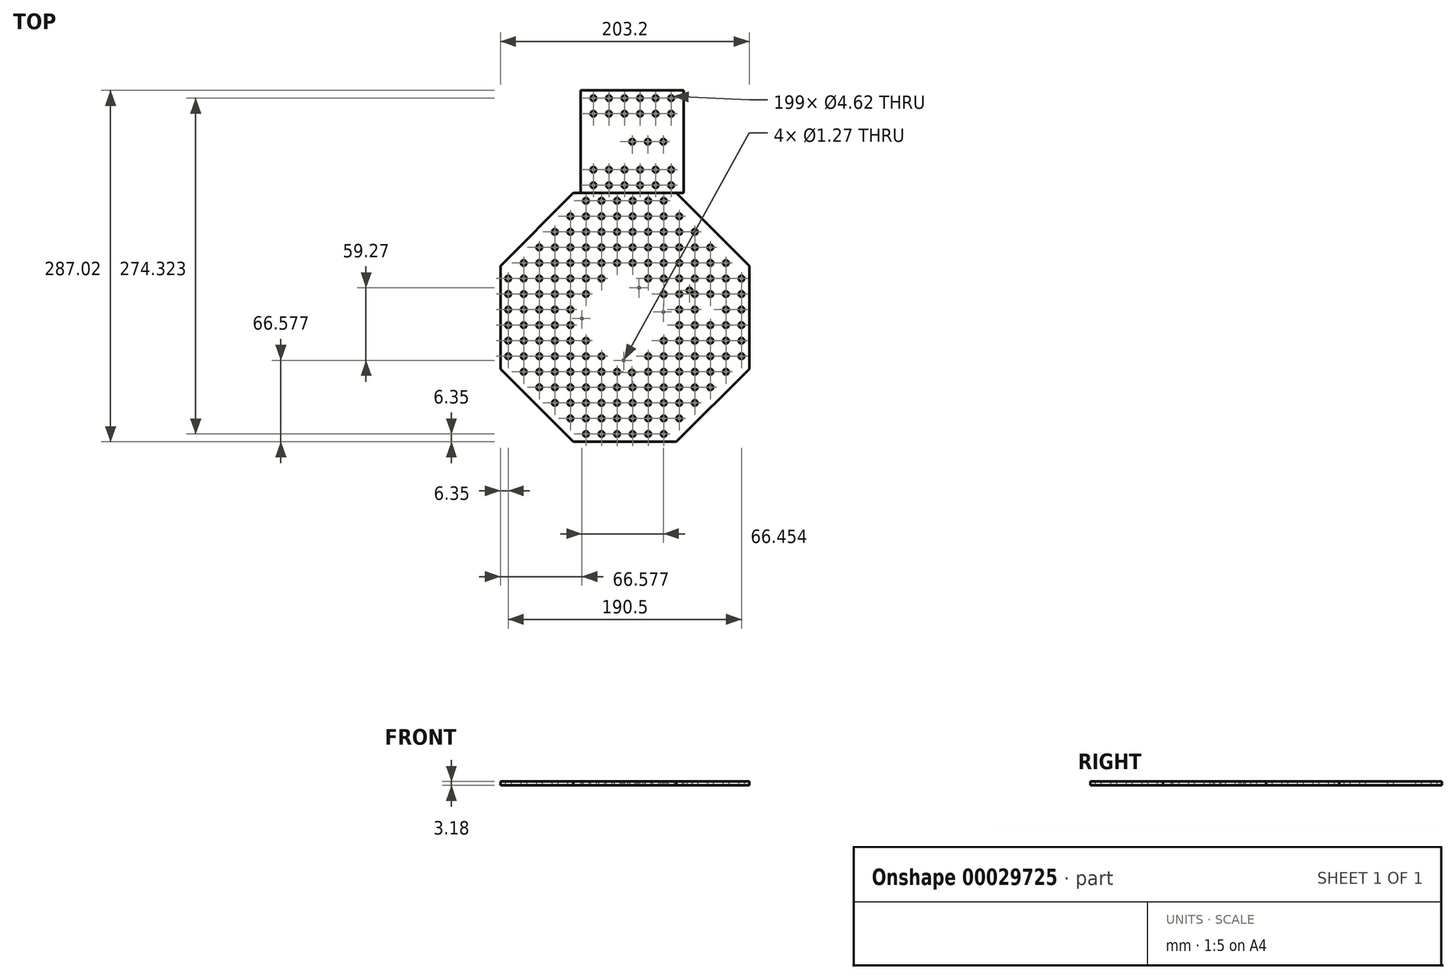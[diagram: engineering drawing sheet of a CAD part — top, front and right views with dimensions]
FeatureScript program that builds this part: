
annotation { "Feature Type Name" : "Feature", "Feature Type Description" : "" }
export const myFeature = defineFeature(function(context is Context, id is Id, definition is map)
    precondition{}
    {
        {
            var Q0;
            Q0=qCreatedBy(makeId("Top.planeOp"),FACE);
            var sketch = newSketch(context, id + "F0", { "sketchPlane" : qUnion([Q0])});
            skLineSegment(sketch, "E0", {"start": v(-101.6, 42.08) * mm, "end": v(-42.08, 101.6) * mm});
            skLineSegment(sketch, "E1", {"start": v(-42.08, 101.6) * mm, "end": v(42.08, 101.6) * mm});
            skLineSegment(sketch, "E2", {"start": v(42.08, 101.6) * mm, "end": v(101.6, 42.08) * mm});
            skLineSegment(sketch, "E3", {"start": v(101.6, 42.08) * mm, "end": v(101.6, -42.08) * mm});
            skLineSegment(sketch, "E4", {"start": v(101.6, -42.08) * mm, "end": v(42.08, -101.6) * mm});
            skLineSegment(sketch, "E5", {"start": v(42.08, -101.6) * mm, "end": v(-42.08, -101.6) * mm});
            skLineSegment(sketch, "E6", {"start": v(-42.08, -101.6) * mm, "end": v(-101.6, -42.08) * mm});
            skLineSegment(sketch, "E7", {"start": v(-101.6, -42.08) * mm, "end": v(-101.6, 42.08) * mm});
            skCircle(sketch, "E8.0.5.0", {"center": v(-95.25, 31.75) * mm, "radius": 2.31 * mm});
            skCircle(sketch, "E8.0.6.0", {"center": v(-95.25, 19.05) * mm, "radius": 2.31 * mm});
            skCircle(sketch, "E8.0.7.0", {"center": v(-95.25, 6.35) * mm, "radius": 2.31 * mm});
            skCircle(sketch, "E8.0.8.0", {"center": v(-95.25, -6.35) * mm, "radius": 2.31 * mm});
            skCircle(sketch, "E8.0.9.0", {"center": v(-95.25, -19.05) * mm, "radius": 2.31 * mm});
            skCircle(sketch, "E8.0.10.0", {"center": v(-95.25, -31.75) * mm, "radius": 2.31 * mm});
            skCircle(sketch, "E8.1.4.0", {"center": v(-82.55, 44.45) * mm, "radius": 2.31 * mm});
            skCircle(sketch, "E8.1.5.0", {"center": v(-82.55, 31.75) * mm, "radius": 2.31 * mm});
            skCircle(sketch, "E8.1.6.0", {"center": v(-82.55, 19.05) * mm, "radius": 2.31 * mm});
            skCircle(sketch, "E8.1.7.0", {"center": v(-82.55, 6.35) * mm, "radius": 2.31 * mm});
            skCircle(sketch, "E8.1.8.0", {"center": v(-82.55, -6.35) * mm, "radius": 2.31 * mm});
            skCircle(sketch, "E8.1.9.0", {"center": v(-82.55, -19.05) * mm, "radius": 2.31 * mm});
            skCircle(sketch, "E8.1.10.0", {"center": v(-82.55, -31.75) * mm, "radius": 2.31 * mm});
            skCircle(sketch, "E8.1.11.0", {"center": v(-82.55, -44.45) * mm, "radius": 2.31 * mm});
            skCircle(sketch, "E8.2.3.0", {"center": v(-69.85, 57.15) * mm, "radius": 2.31 * mm});
            skCircle(sketch, "E8.2.4.0", {"center": v(-69.85, 44.45) * mm, "radius": 2.31 * mm});
            skCircle(sketch, "E8.2.5.0", {"center": v(-69.85, 31.75) * mm, "radius": 2.31 * mm});
            skCircle(sketch, "E8.2.6.0", {"center": v(-69.85, 19.05) * mm, "radius": 2.31 * mm});
            skCircle(sketch, "E8.2.7.0", {"center": v(-69.85, 6.35) * mm, "radius": 2.31 * mm});
            skCircle(sketch, "E8.2.8.0", {"center": v(-69.85, -6.35) * mm, "radius": 2.31 * mm});
            skCircle(sketch, "E8.2.9.0", {"center": v(-69.85, -19.05) * mm, "radius": 2.31 * mm});
            skCircle(sketch, "E8.2.10.0", {"center": v(-69.85, -31.75) * mm, "radius": 2.31 * mm});
            skCircle(sketch, "E8.2.11.0", {"center": v(-69.85, -44.45) * mm, "radius": 2.31 * mm});
            skCircle(sketch, "E8.2.12.0", {"center": v(-69.85, -57.15) * mm, "radius": 2.31 * mm});
            skCircle(sketch, "E8.3.2.0", {"center": v(-57.15, 69.85) * mm, "radius": 2.31 * mm});
            skCircle(sketch, "E8.3.3.0", {"center": v(-57.15, 57.15) * mm, "radius": 2.31 * mm});
            skCircle(sketch, "E8.3.4.0", {"center": v(-57.15, 44.45) * mm, "radius": 2.31 * mm});
            skCircle(sketch, "E8.3.5.0", {"center": v(-57.15, 31.75) * mm, "radius": 2.31 * mm});
            skCircle(sketch, "E8.3.6.0", {"center": v(-57.15, 19.05) * mm, "radius": 2.31 * mm});
            skCircle(sketch, "E8.3.7.0", {"center": v(-57.15, 6.35) * mm, "radius": 2.31 * mm});
            skCircle(sketch, "E8.3.8.0", {"center": v(-57.15, -6.35) * mm, "radius": 2.31 * mm});
            skCircle(sketch, "E8.3.9.0", {"center": v(-57.15, -19.05) * mm, "radius": 2.31 * mm});
            skCircle(sketch, "E8.3.10.0", {"center": v(-57.15, -31.75) * mm, "radius": 2.31 * mm});
            skCircle(sketch, "E8.3.11.0", {"center": v(-57.15, -44.45) * mm, "radius": 2.31 * mm});
            skCircle(sketch, "E8.3.12.0", {"center": v(-57.15, -57.15) * mm, "radius": 2.31 * mm});
            skCircle(sketch, "E8.3.13.0", {"center": v(-57.15, -69.85) * mm, "radius": 2.31 * mm});
            skCircle(sketch, "E8.4.1.0", {"center": v(-44.45, 82.55) * mm, "radius": 2.31 * mm});
            skCircle(sketch, "E8.4.2.0", {"center": v(-44.45, 69.85) * mm, "radius": 2.31 * mm});
            skCircle(sketch, "E8.4.3.0", {"center": v(-44.45, 57.15) * mm, "radius": 2.31 * mm});
            skCircle(sketch, "E8.4.4.0", {"center": v(-44.45, 44.45) * mm, "radius": 2.31 * mm});
            skCircle(sketch, "E8.4.5.0", {"center": v(-44.45, 31.75) * mm, "radius": 2.31 * mm});
            skCircle(sketch, "E8.4.6.0", {"center": v(-44.45, 19.05) * mm, "radius": 2.31 * mm});
            skCircle(sketch, "E8.4.7.0", {"center": v(-44.45, 6.35) * mm, "radius": 2.31 * mm});
            skCircle(sketch, "E8.4.8.0", {"center": v(-44.45, -6.35) * mm, "radius": 2.31 * mm});
            skCircle(sketch, "E8.4.9.0", {"center": v(-44.45, -19.05) * mm, "radius": 2.31 * mm});
            skCircle(sketch, "E8.4.10.0", {"center": v(-44.45, -31.75) * mm, "radius": 2.31 * mm});
            skCircle(sketch, "E8.4.11.0", {"center": v(-44.45, -44.45) * mm, "radius": 2.31 * mm});
            skCircle(sketch, "E8.4.12.0", {"center": v(-44.45, -57.15) * mm, "radius": 2.31 * mm});
            skCircle(sketch, "E8.4.13.0", {"center": v(-44.45, -69.85) * mm, "radius": 2.31 * mm});
            skCircle(sketch, "E8.4.14.0", {"center": v(-44.45, -82.55) * mm, "radius": 2.31 * mm});
            skCircle(sketch, "E8.5.0.0", {"center": v(-31.75, 95.25) * mm, "radius": 2.31 * mm});
            skCircle(sketch, "E8.5.1.0", {"center": v(-31.75, 82.55) * mm, "radius": 2.31 * mm});
            skCircle(sketch, "E8.5.2.0", {"center": v(-31.75, 69.85) * mm, "radius": 2.31 * mm});
            skCircle(sketch, "E8.5.3.0", {"center": v(-31.75, 57.15) * mm, "radius": 2.31 * mm});
            skCircle(sketch, "E8.5.4.0", {"center": v(-31.75, 44.45) * mm, "radius": 2.31 * mm});
            skCircle(sketch, "E8.5.5.0", {"center": v(-31.75, 31.75) * mm, "radius": 2.31 * mm});
            skCircle(sketch, "E8.5.6.0", {"center": v(-31.75, 19.05) * mm, "radius": 2.31 * mm});
            skCircle(sketch, "E8.5.9.0", {"center": v(-31.75, -19.05) * mm, "radius": 2.31 * mm});
            skCircle(sketch, "E8.5.10.0", {"center": v(-31.75, -31.75) * mm, "radius": 2.31 * mm});
            skCircle(sketch, "E8.5.11.0", {"center": v(-31.75, -44.45) * mm, "radius": 2.31 * mm});
            skCircle(sketch, "E8.5.12.0", {"center": v(-31.75, -57.15) * mm, "radius": 2.31 * mm});
            skCircle(sketch, "E8.5.13.0", {"center": v(-31.75, -69.85) * mm, "radius": 2.31 * mm});
            skCircle(sketch, "E8.5.14.0", {"center": v(-31.75, -82.55) * mm, "radius": 2.31 * mm});
            skCircle(sketch, "E8.5.15.0", {"center": v(-31.75, -95.25) * mm, "radius": 2.31 * mm});
            skCircle(sketch, "E8.6.0.0", {"center": v(-19.05, 95.25) * mm, "radius": 2.31 * mm});
            skCircle(sketch, "E8.6.1.0", {"center": v(-19.05, 82.55) * mm, "radius": 2.31 * mm});
            skCircle(sketch, "E8.6.2.0", {"center": v(-19.05, 69.85) * mm, "radius": 2.31 * mm});
            skCircle(sketch, "E8.6.3.0", {"center": v(-19.05, 57.15) * mm, "radius": 2.31 * mm});
            skCircle(sketch, "E8.6.4.0", {"center": v(-19.05, 44.45) * mm, "radius": 2.31 * mm});
            skCircle(sketch, "E8.6.5.0", {"center": v(-19.05, 31.75) * mm, "radius": 2.31 * mm});
            skCircle(sketch, "E8.6.10.0", {"center": v(-19.05, -31.75) * mm, "radius": 2.31 * mm});
            skCircle(sketch, "E8.6.11.0", {"center": v(-19.05, -44.45) * mm, "radius": 2.31 * mm});
            skCircle(sketch, "E8.6.12.0", {"center": v(-19.05, -57.15) * mm, "radius": 2.31 * mm});
            skCircle(sketch, "E8.6.13.0", {"center": v(-19.05, -69.85) * mm, "radius": 2.31 * mm});
            skCircle(sketch, "E8.6.14.0", {"center": v(-19.05, -82.55) * mm, "radius": 2.31 * mm});
            skCircle(sketch, "E8.6.15.0", {"center": v(-19.05, -95.25) * mm, "radius": 2.31 * mm});
            skCircle(sketch, "E8.7.0.0", {"center": v(-6.35, 95.25) * mm, "radius": 2.31 * mm});
            skCircle(sketch, "E8.7.1.0", {"center": v(-6.35, 82.55) * mm, "radius": 2.31 * mm});
            skCircle(sketch, "E8.7.2.0", {"center": v(-6.35, 69.85) * mm, "radius": 2.31 * mm});
            skCircle(sketch, "E8.7.3.0", {"center": v(-6.35, 57.15) * mm, "radius": 2.31 * mm});
            skCircle(sketch, "E8.7.4.0", {"center": v(-6.35, 44.45) * mm, "radius": 2.31 * mm});
            skCircle(sketch, "E8.7.11.0", {"center": v(-6.35, -44.45) * mm, "radius": 2.31 * mm});
            skCircle(sketch, "E8.7.12.0", {"center": v(-6.35, -57.15) * mm, "radius": 2.31 * mm});
            skCircle(sketch, "E8.7.13.0", {"center": v(-6.35, -69.85) * mm, "radius": 2.31 * mm});
            skCircle(sketch, "E8.7.14.0", {"center": v(-6.35, -82.55) * mm, "radius": 2.31 * mm});
            skCircle(sketch, "E8.7.15.0", {"center": v(-6.35, -95.25) * mm, "radius": 2.31 * mm});
            skCircle(sketch, "E8.8.0.0", {"center": v(6.35, 95.25) * mm, "radius": 2.31 * mm});
            skCircle(sketch, "E8.8.1.0", {"center": v(6.35, 82.55) * mm, "radius": 2.31 * mm});
            skCircle(sketch, "E8.8.2.0", {"center": v(6.35, 69.85) * mm, "radius": 2.31 * mm});
            skCircle(sketch, "E8.8.3.0", {"center": v(6.35, 57.15) * mm, "radius": 2.31 * mm});
            skCircle(sketch, "E8.8.4.0", {"center": v(6.35, 44.45) * mm, "radius": 2.31 * mm});
            skCircle(sketch, "E8.8.11.0", {"center": v(5.77, -44.96) * mm, "radius": 2.31 * mm});
            skCircle(sketch, "E8.8.12.0", {"center": v(6.35, -57.15) * mm, "radius": 2.31 * mm});
            skCircle(sketch, "E8.8.13.0", {"center": v(6.35, -69.85) * mm, "radius": 2.31 * mm});
            skCircle(sketch, "E8.8.14.0", {"center": v(6.35, -82.55) * mm, "radius": 2.31 * mm});
            skCircle(sketch, "E8.8.15.0", {"center": v(6.35, -95.25) * mm, "radius": 2.31 * mm});
            skCircle(sketch, "E8.9.0.0", {"center": v(19.05, 95.25) * mm, "radius": 2.31 * mm});
            skCircle(sketch, "E8.9.1.0", {"center": v(19.05, 82.55) * mm, "radius": 2.31 * mm});
            skCircle(sketch, "E8.9.2.0", {"center": v(19.05, 69.85) * mm, "radius": 2.31 * mm});
            skCircle(sketch, "E8.9.3.0", {"center": v(19.05, 57.15) * mm, "radius": 2.31 * mm});
            skCircle(sketch, "E8.9.4.0", {"center": v(19.05, 44.45) * mm, "radius": 2.31 * mm});
            skCircle(sketch, "E8.9.5.0", {"center": v(19.05, 31.75) * mm, "radius": 2.31 * mm});
            skCircle(sketch, "E8.9.10.0", {"center": v(19.05, -31.75) * mm, "radius": 2.31 * mm});
            skCircle(sketch, "E8.9.11.0", {"center": v(19.05, -44.45) * mm, "radius": 2.31 * mm});
            skCircle(sketch, "E8.9.12.0", {"center": v(19.05, -57.15) * mm, "radius": 2.31 * mm});
            skCircle(sketch, "E8.9.13.0", {"center": v(19.05, -69.85) * mm, "radius": 2.31 * mm});
            skCircle(sketch, "E8.9.14.0", {"center": v(19.05, -82.55) * mm, "radius": 2.31 * mm});
            skCircle(sketch, "E8.9.15.0", {"center": v(19.05, -95.25) * mm, "radius": 2.31 * mm});
            skCircle(sketch, "E8.10.0.0", {"center": v(31.75, 95.25) * mm, "radius": 2.31 * mm});
            skCircle(sketch, "E8.10.1.0", {"center": v(31.75, 82.55) * mm, "radius": 2.31 * mm});
            skCircle(sketch, "E8.10.2.0", {"center": v(31.75, 69.85) * mm, "radius": 2.31 * mm});
            skCircle(sketch, "E8.10.3.0", {"center": v(31.75, 57.15) * mm, "radius": 2.31 * mm});
            skCircle(sketch, "E8.10.4.0", {"center": v(31.75, 44.45) * mm, "radius": 2.31 * mm});
            skCircle(sketch, "E8.10.5.0", {"center": v(31.75, 31.75) * mm, "radius": 2.31 * mm});
            skCircle(sketch, "E8.10.6.0", {"center": v(31.75, 19.05) * mm, "radius": 2.31 * mm});
            skCircle(sketch, "E8.10.9.0", {"center": v(31.75, -19.05) * mm, "radius": 2.31 * mm});
            skCircle(sketch, "E8.10.10.0", {"center": v(31.75, -31.75) * mm, "radius": 2.31 * mm});
            skCircle(sketch, "E8.10.11.0", {"center": v(31.75, -44.45) * mm, "radius": 2.31 * mm});
            skCircle(sketch, "E8.10.12.0", {"center": v(31.75, -57.15) * mm, "radius": 2.31 * mm});
            skCircle(sketch, "E8.10.13.0", {"center": v(31.75, -69.85) * mm, "radius": 2.31 * mm});
            skCircle(sketch, "E8.10.14.0", {"center": v(31.75, -82.55) * mm, "radius": 2.31 * mm});
            skCircle(sketch, "E8.10.15.0", {"center": v(31.75, -95.25) * mm, "radius": 2.31 * mm});
            skCircle(sketch, "E8.11.1.0", {"center": v(44.45, 82.55) * mm, "radius": 2.31 * mm});
            skCircle(sketch, "E8.11.2.0", {"center": v(44.45, 69.85) * mm, "radius": 2.31 * mm});
            skCircle(sketch, "E8.11.3.0", {"center": v(44.45, 57.15) * mm, "radius": 2.31 * mm});
            skCircle(sketch, "E8.11.4.0", {"center": v(44.45, 44.45) * mm, "radius": 2.31 * mm});
            skCircle(sketch, "E8.11.5.0", {"center": v(44.45, 31.75) * mm, "radius": 2.31 * mm});
            skCircle(sketch, "E8.11.6.0", {"center": v(44.45, 19.05) * mm, "radius": 2.31 * mm});
            skCircle(sketch, "E8.11.7.0", {"center": v(44.45, 6.35) * mm, "radius": 2.31 * mm});
            skCircle(sketch, "E8.11.8.0", {"center": v(44.45, -6.35) * mm, "radius": 2.31 * mm});
            skCircle(sketch, "E8.11.9.0", {"center": v(44.45, -19.05) * mm, "radius": 2.31 * mm});
            skCircle(sketch, "E8.11.10.0", {"center": v(44.45, -31.75) * mm, "radius": 2.31 * mm});
            skCircle(sketch, "E8.11.11.0", {"center": v(44.45, -44.45) * mm, "radius": 2.31 * mm});
            skCircle(sketch, "E8.11.12.0", {"center": v(44.45, -57.15) * mm, "radius": 2.31 * mm});
            skCircle(sketch, "E8.11.13.0", {"center": v(44.45, -69.85) * mm, "radius": 2.31 * mm});
            skCircle(sketch, "E8.11.14.0", {"center": v(44.45, -82.55) * mm, "radius": 2.31 * mm});
            skCircle(sketch, "E8.12.2.0", {"center": v(57.15, 69.85) * mm, "radius": 2.31 * mm});
            skCircle(sketch, "E8.12.3.0", {"center": v(57.15, 57.15) * mm, "radius": 2.31 * mm});
            skCircle(sketch, "E8.12.4.0", {"center": v(57.15, 44.45) * mm, "radius": 2.31 * mm});
            skCircle(sketch, "E8.12.5.0", {"center": v(57.15, 31.75) * mm, "radius": 2.31 * mm});
            skCircle(sketch, "E8.12.6.0", {"center": v(57.15, 19.05) * mm, "radius": 2.31 * mm});
            skCircle(sketch, "E8.12.7.0", {"center": v(57.15, 6.35) * mm, "radius": 2.31 * mm});
            skCircle(sketch, "E8.12.8.0", {"center": v(57.15, -6.35) * mm, "radius": 2.31 * mm});
            skCircle(sketch, "E8.12.9.0", {"center": v(57.15, -19.05) * mm, "radius": 2.31 * mm});
            skCircle(sketch, "E8.12.10.0", {"center": v(57.15, -31.75) * mm, "radius": 2.31 * mm});
            skCircle(sketch, "E8.12.11.0", {"center": v(57.15, -44.45) * mm, "radius": 2.31 * mm});
            skCircle(sketch, "E8.12.12.0", {"center": v(57.15, -57.15) * mm, "radius": 2.31 * mm});
            skCircle(sketch, "E8.12.13.0", {"center": v(57.15, -69.85) * mm, "radius": 2.31 * mm});
            skCircle(sketch, "E8.13.3.0", {"center": v(69.85, 57.15) * mm, "radius": 2.31 * mm});
            skCircle(sketch, "E8.13.4.0", {"center": v(69.85, 44.45) * mm, "radius": 2.31 * mm});
            skCircle(sketch, "E8.13.5.0", {"center": v(69.85, 31.75) * mm, "radius": 2.31 * mm});
            skCircle(sketch, "E8.13.6.0", {"center": v(69.85, 19.05) * mm, "radius": 2.31 * mm});
            skCircle(sketch, "E8.13.7.0", {"center": v(52.82, 21.97) * mm, "radius": 2.31 * mm});
            skCircle(sketch, "E8.13.8.0", {"center": v(69.85, -6.35) * mm, "radius": 2.31 * mm});
            skCircle(sketch, "E8.13.9.0", {"center": v(69.85, -19.05) * mm, "radius": 2.31 * mm});
            skCircle(sketch, "E8.13.10.0", {"center": v(69.85, -31.75) * mm, "radius": 2.31 * mm});
            skCircle(sketch, "E8.13.11.0", {"center": v(69.85, -44.45) * mm, "radius": 2.31 * mm});
            skCircle(sketch, "E8.13.12.0", {"center": v(69.85, -57.15) * mm, "radius": 2.31 * mm});
            skCircle(sketch, "E8.14.4.0", {"center": v(82.55, 44.45) * mm, "radius": 2.31 * mm});
            skCircle(sketch, "E8.14.5.0", {"center": v(82.55, 31.75) * mm, "radius": 2.31 * mm});
            skCircle(sketch, "E8.14.6.0", {"center": v(82.55, 19.05) * mm, "radius": 2.31 * mm});
            skCircle(sketch, "E8.14.7.0", {"center": v(82.55, 6.35) * mm, "radius": 2.31 * mm});
            skCircle(sketch, "E8.14.8.0", {"center": v(82.55, -6.35) * mm, "radius": 2.31 * mm});
            skCircle(sketch, "E8.14.9.0", {"center": v(82.55, -19.05) * mm, "radius": 2.31 * mm});
            skCircle(sketch, "E8.14.10.0", {"center": v(82.55, -31.75) * mm, "radius": 2.31 * mm});
            skCircle(sketch, "E8.14.11.0", {"center": v(82.55, -44.45) * mm, "radius": 2.31 * mm});
            skCircle(sketch, "E8.15.5.0", {"center": v(95.25, 31.75) * mm, "radius": 2.31 * mm});
            skCircle(sketch, "E8.15.6.0", {"center": v(95.25, 19.05) * mm, "radius": 2.31 * mm});
            skCircle(sketch, "E8.15.7.0", {"center": v(95.25, 6.35) * mm, "radius": 2.31 * mm});
            skCircle(sketch, "E8.15.8.0", {"center": v(95.25, -6.35) * mm, "radius": 2.31 * mm});
            skCircle(sketch, "E8.15.9.0", {"center": v(95.25, -19.05) * mm, "radius": 2.31 * mm});
            skCircle(sketch, "E8.15.10.0", {"center": v(95.25, -31.75) * mm, "radius": 2.31 * mm});
            skPoint(sketch, "E9", {"position": v(-25.4, 88.9) * mm});
            skPoint(sketch, "E10", {"position": v(-101.6, 88.9) * mm});
            skPoint(sketch, "E11", {"position": v(-88.9, 88.9) * mm});
            skPoint(sketch, "E12", {"position": v(-71.84, -71.84) * mm});
            skPoint(sketch, "E13", {"position": v(71.84, 71.84) * mm});
            skPoint(sketch, "E14", {"position": v(0, 0) * mm});
            skCircle(sketch, "E15", {"center": v(-35.02, -0.9) * mm, "radius": 0.64 * mm});
            skCircle(sketch, "E16", {"center": v(-0.9, -35.02) * mm, "radius": 0.64 * mm});
            skCircle(sketch, "E17", {"center": v(31.43, 4.5) * mm, "radius": 0.64 * mm});
            skCircle(sketch, "E18", {"center": v(11.67, 24.25) * mm, "radius": 0.64 * mm});
            skPoint(sketch, "E19", {"position": v(-42.08, 101.6) * mm});
            skPoint(sketch, "E20", {"position": v(42.08, 101.6) * mm});
            skSolve(sketch);
        }
        {
            var Q0;
            Q0=qCreatedBy(makeId("Top.planeOp"),FACE);
            var sketch = newSketch(context, id + "F1", { "sketchPlane" : qUnion([Q0])});
            skLineSegment(sketch, "E21", {"start": v(-36.01, 101.6) * mm, "end": v(48.16, 101.6) * mm});
            skLineSegment(sketch, "E22", {"start": v(48.16, 101.6) * mm, "end": v(48.16, 185.42) * mm});
            skLineSegment(sketch, "E23", {"start": v(48.16, 185.42) * mm, "end": v(-36.01, 185.42) * mm});
            skLineSegment(sketch, "E24", {"start": v(-36.01, 101.6) * mm, "end": v(-36.01, 185.42) * mm});
            skPoint(sketch, "E25", {"position": v(37.83, 101.6) * mm});
            skPoint(sketch, "E26", {"position": v(37.83, 107.95) * mm});
            skCircle(sketch, "E27", {"center": v(37.83, 107.95) * mm, "radius": 2.31 * mm});
            skLineSegment(sketch, "E28.direction1", {"start": v(37.83, 107.95) * mm, "end": v(25.13, 107.95) * mm, "construction": true});
            skLineSegment(sketch, "E28.direction2", {"start": v(37.83, 107.95) * mm, "end": v(37.83, 120.65) * mm, "construction": true});
            skLineSegment(sketch, "E29.direction1", {"start": v(6.08, 146.05) * mm, "end": v(18.78, 146.05) * mm, "construction": true});
            skPoint(sketch, "E30.endSnap0", {"position": v(-36.01, 143.51) * mm});
            skPoint(sketch, "E31", {"position": v(6.08, 143.51) * mm});
            skPoint(sketch, "E32", {"position": v(37.83, 179.07) * mm});
            skCircle(sketch, "E33", {"center": v(6.08, 143.51) * mm, "radius": 2.31 * mm});
            skCircle(sketch, "E34", {"center": v(37.83, 179.07) * mm, "radius": 2.31 * mm});
            skCircle(sketch, "E35.1.0.0", {"center": v(18.78, 143.51) * mm, "radius": 2.31 * mm});
            skCircle(sketch, "E35.2.0.0", {"center": v(31.48, 143.51) * mm, "radius": 2.31 * mm});
            skLineSegment(sketch, "E35.direction1", {"start": v(6.08, 143.51) * mm, "end": v(18.78, 143.51) * mm, "construction": true});
            skLineSegment(sketch, "E36.direction1", {"start": v(37.83, 179.07) * mm, "end": v(25.13, 179.07) * mm, "construction": true});
            skCircle(sketch, "E37.0.1.0", {"center": v(37.83, 120.65) * mm, "radius": 2.31 * mm});
            skCircle(sketch, "E37.1.0.0", {"center": v(25.13, 107.95) * mm, "radius": 2.31 * mm});
            skCircle(sketch, "E37.1.1.0", {"center": v(25.13, 120.65) * mm, "radius": 2.31 * mm});
            skCircle(sketch, "E37.2.0.0", {"center": v(12.43, 107.95) * mm, "radius": 2.31 * mm});
            skCircle(sketch, "E37.2.1.0", {"center": v(12.43, 120.65) * mm, "radius": 2.31 * mm});
            skCircle(sketch, "E37.3.0.0", {"center": v(-0.27, 107.95) * mm, "radius": 2.31 * mm});
            skCircle(sketch, "E37.3.1.0", {"center": v(-0.27, 120.65) * mm, "radius": 2.31 * mm});
            skCircle(sketch, "E37.4.0.0", {"center": v(-12.97, 107.95) * mm, "radius": 2.31 * mm});
            skCircle(sketch, "E37.4.1.0", {"center": v(-12.97, 120.65) * mm, "radius": 2.31 * mm});
            skCircle(sketch, "E37.5.0.0", {"center": v(-25.67, 107.95) * mm, "radius": 2.31 * mm});
            skCircle(sketch, "E37.5.1.0", {"center": v(-25.67, 120.65) * mm, "radius": 2.31 * mm});
            skCircle(sketch, "E38.0.1.0", {"center": v(37.83, 166.37) * mm, "radius": 2.31 * mm});
            skCircle(sketch, "E38.1.0.0", {"center": v(25.13, 179.07) * mm, "radius": 2.31 * mm});
            skCircle(sketch, "E38.1.1.0", {"center": v(25.13, 166.37) * mm, "radius": 2.31 * mm});
            skCircle(sketch, "E38.2.0.0", {"center": v(12.43, 179.07) * mm, "radius": 2.31 * mm});
            skCircle(sketch, "E38.2.1.0", {"center": v(12.43, 166.37) * mm, "radius": 2.31 * mm});
            skCircle(sketch, "E38.3.0.0", {"center": v(-0.27, 179.07) * mm, "radius": 2.31 * mm});
            skCircle(sketch, "E38.3.1.0", {"center": v(-0.27, 166.37) * mm, "radius": 2.31 * mm});
            skCircle(sketch, "E38.4.0.0", {"center": v(-12.97, 179.07) * mm, "radius": 2.31 * mm});
            skCircle(sketch, "E38.4.1.0", {"center": v(-12.97, 166.37) * mm, "radius": 2.31 * mm});
            skCircle(sketch, "E38.5.0.0", {"center": v(-25.67, 179.07) * mm, "radius": 2.31 * mm});
            skCircle(sketch, "E38.5.1.0", {"center": v(-25.67, 166.37) * mm, "radius": 2.31 * mm});
            skLineSegment(sketch, "E38.direction2", {"start": v(37.83, 179.07) * mm, "end": v(37.83, 166.37) * mm, "construction": true});
            skSolve(sketch);
        }
        {
            var Q0;
            Q0=makeQuery(id+"F0.imprint","IMPRINT",FACE,{"disambiguationData":[TD([[makeQuery(id+"F0.imprint","IMPRINT",EDGE,{"derivedFrom":sQuery(id+"F0.wireOp",EDGE,"E0")}),-1.0]])]});
            extrude(context, id + "F2", {"entities" : qUnion([Q0]), "depth" : 3.17 * mm});
        }
        {
            var Q0;
            Q0=makeQuery(id+"F1.imprint","IMPRINT",FACE,{"disambiguationData":[TD([[makeQuery(id+"F1.imprint","IMPRINT",EDGE,{"derivedFrom":sQuery(id+"F1.wireOp",EDGE,"E21")}),1.0]])]});
            extrude(context, id + "F3", {"entities" : qUnion([Q0]), "depth" : 3.17 * mm});
        }
    });
